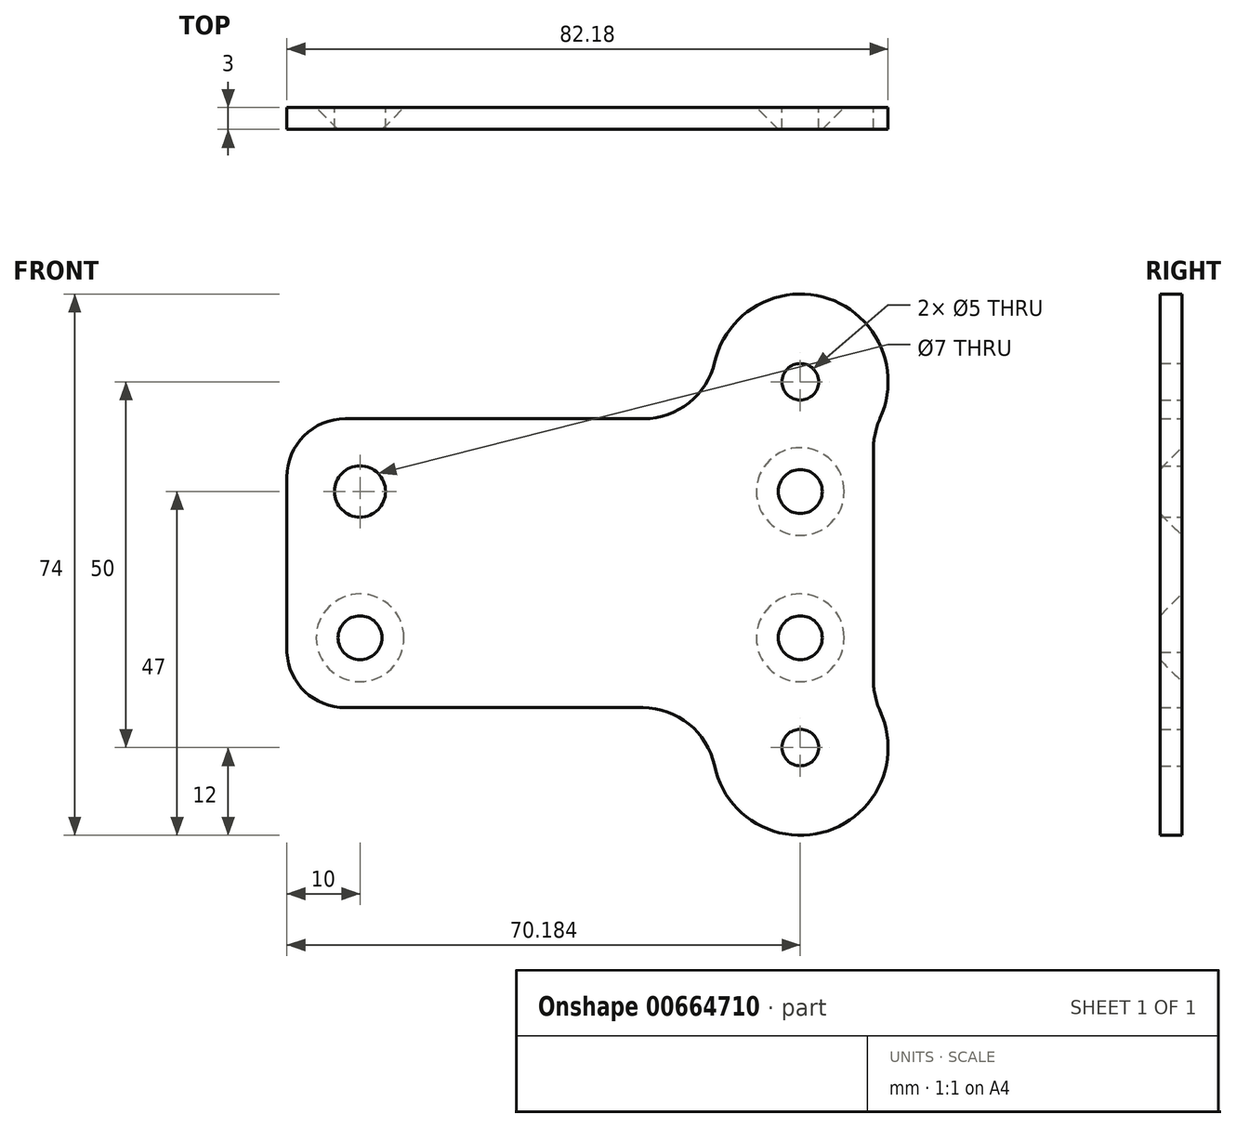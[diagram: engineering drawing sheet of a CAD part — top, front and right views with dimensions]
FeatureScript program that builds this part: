
annotation { "Feature Type Name" : "Feature", "Feature Type Description" : "" }
export const myFeature = defineFeature(function(context is Context, id is Id, definition is map)
    precondition{}
    {
        {
            var Q0;
            Q0=qCreatedBy(makeId("Front.planeOp"),FACE);
            var sketch = newSketch(context, id + "F0", { "sketchPlane" : qUnion([Q0])});
            skPoint(sketch, "E0.middle", {"position": v(0, 0) * mm});
            skLineSegment(sketch, "E1.0", {"start": v(50, 10) * mm, "end": v(-50, 10) * mm, "construction": true});
            skLineSegment(sketch, "E2.0", {"start": v(50, -10) * mm, "end": v(-50, -10) * mm, "construction": true});
            skLineSegment(sketch, "E3.0", {"start": v(50, 25) * mm, "end": v(-50, 25) * mm, "construction": true});
            skLineSegment(sketch, "E4.0", {"start": v(50, -25) * mm, "end": v(-50, -25) * mm, "construction": true});
            skLineSegment(sketch, "E5.0", {"start": v(30.18, 49.26) * mm, "end": v(30.18, -50.74) * mm, "construction": true});
            skLineSegment(sketch, "E6.0", {"start": v(-30, 50) * mm, "end": v(-30, -50) * mm, "construction": true});
            skCircle(sketch, "E7", {"center": v(30.18, 25) * mm, "radius": 2.5 * mm});
            skCircle(sketch, "E8", {"center": v(30.18, -25) * mm, "radius": 2.5 * mm});
            skArc(sketch, "E9", {"start": v(18.44, -27.49) * mm, "mid": v(33.95, -36.4) * mm, "end": v(41.1, -20) * mm});
            skArc(sketch, "E10", {"start": v(41.1, 20) * mm, "mid": v(34.06, 36.36) * mm, "end": v(18.5, 27.7) * mm});
            skCircle(sketch, "E11", {"center": v(-30, -10) * mm, "radius": 2.5 * mm});
            skCircle(sketch, "E12", {"center": v(-30, 10) * mm, "radius": 3.5 * mm});
            skCircle(sketch, "E13", {"center": v(30.18, 10) * mm, "radius": 2.5 * mm});
            skCircle(sketch, "E14", {"center": v(30.18, -10) * mm, "radius": 2.5 * mm});
            skLineSegment(sketch, "E15", {"start": v(-32.01, -19.56) * mm, "end": v(8.66, -19.56) * mm, "construction": true});
            skLineSegment(sketch, "E16", {"start": v(-32.01, -19.56) * mm, "end": v(8.66, -19.56) * mm});
            skArc(sketch, "E17.filletArc", {"start": v(8.75, 19.96) * mm, "mid": v(14.97, 22.13) * mm, "end": v(18.5, 27.7) * mm});
            skArc(sketch, "E18.filletArc", {"start": v(-40, -12) * mm, "mid": v(-37.51, -17.37) * mm, "end": v(-32.01, -19.56) * mm});
            skArc(sketch, "E19.filletArc", {"start": v(18.44, -27.49) * mm, "mid": v(14.96, -21.79) * mm, "end": v(8.66, -19.56) * mm});
            skLineSegment(sketch, "E20", {"start": v(8.75, 19.96) * mm, "end": v(-32, 19.96) * mm});
            skLineSegment(sketch, "E21", {"start": v(-40, -12) * mm, "end": v(-40, 11.96) * mm});
            skArc(sketch, "E22.filletArc", {"start": v(-32, 19.96) * mm, "mid": v(-37.66, 17.62) * mm, "end": v(-40, 11.96) * mm});
            skLineSegment(sketch, "E23.0", {"start": v(40.18, 15.83) * mm, "end": v(40.18, -15.83) * mm, "construction": true});
            skLineSegment(sketch, "E24", {"start": v(40.18, 15.83) * mm, "end": v(40.18, -15.83) * mm});
            skArc(sketch, "E25.filletArc", {"start": v(41.1, 20) * mm, "mid": v(40.41, 17.97) * mm, "end": v(40.18, 15.83) * mm});
            skArc(sketch, "E26.filletArc", {"start": v(40.18, -15.83) * mm, "mid": v(40.41, -17.97) * mm, "end": v(41.1, -20) * mm});
            skLineSegment(sketch, "E27", {"start": v(-40, 37) * mm, "end": v(42.18, 37) * mm, "construction": true});
            skLineSegment(sketch, "E28", {"start": v(-40, -37) * mm, "end": v(42.18, -37) * mm, "construction": true});
            skLineSegment(sketch, "E29", {"start": v(-40, 37) * mm, "end": v(-40, -37) * mm, "construction": true});
            skLineSegment(sketch, "E30", {"start": v(42.18, 37) * mm, "end": v(42.18, -37) * mm, "construction": true});
            skSolve(sketch);
        }
        {
            var Q0;
            Q0=makeQuery(id+"F0.imprint","IMPRINT",FACE,{"disambiguationData":[TD([[makeQuery(id+"F0.imprint","IMPRINT",EDGE,{"derivedFrom":sQuery(id+"F0.wireOp",EDGE,"E7")}),-1.0]])]});
            extrude(context, id + "F1", {"entities" : qUnion([Q0]), "depth" : 3 * mm, "offsetDistance" : 25 * mm});
        }
        {
            var Q0;
            Q0=makeQuery(id+"F1.opExtrude","CAP_EDGE",EDGE,{"disambiguationData":[OSD([sQuery(id+"F0.wireOp",EDGE,"E13")])],"isStart":true});
            var Q1;
            Q1=makeQuery(id+"F1.opExtrude","CAP_EDGE",EDGE,{"disambiguationData":[OSD([sQuery(id+"F0.wireOp",EDGE,"E14")])],"isStart":true});
            var Q2;
            Q2=makeQuery(id+"F1.opExtrude","CAP_EDGE",EDGE,{"disambiguationData":[OSD([sQuery(id+"F0.wireOp",EDGE,"E11")])],"isStart":true});
            chamfer(context, id + "F2", {"entities" : qUnion([Q0, Q1, Q2]), "width" : 3.5 * mm, "tangentPropagation" : true});
        }
    });
